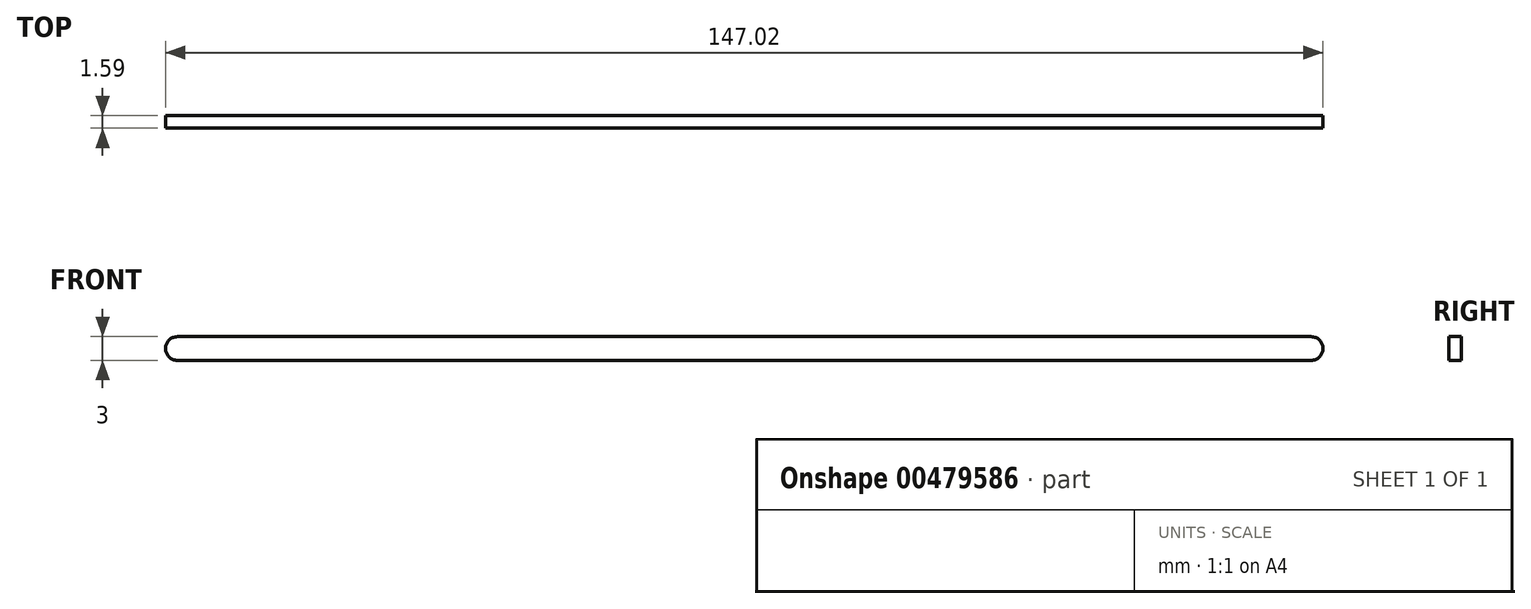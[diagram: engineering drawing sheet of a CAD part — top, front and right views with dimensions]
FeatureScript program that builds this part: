
annotation { "Feature Type Name" : "Feature", "Feature Type Description" : "" }
export const myFeature = defineFeature(function(context is Context, id is Id, definition is map)
    precondition{}
    {
        {
            var Q0;
            Q0=qCreatedBy(makeId("Front.planeOp"),FACE);
            var sketch = newSketch(context, id + "F0", { "sketchPlane" : qUnion([Q0])});
            skLineSegment(sketch, "E0.bottom", {"start": v(72, -1.5) * mm, "end": v(-72, -1.5) * mm});
            skLineSegment(sketch, "E0.top", {"start": v(72, 1.5) * mm, "end": v(-72, 1.5) * mm});
            skPoint(sketch, "E0.middle", {"position": v(0, 0) * mm});
            skArc(sketch, "E1", {"start": v(72, -1.5) * mm, "mid": v(73.5, 0) * mm, "end": v(72, 1.5) * mm});
            skArc(sketch, "E2", {"start": v(-72, 1.5) * mm, "mid": v(-73.5, 0) * mm, "end": v(-72, -1.5) * mm});
            skSolve(sketch);
        }
        {
            var Q0;
            Q0=makeQuery(id+"F0.imprint","IMPRINT",FACE,{"disambiguationData":[TD([[makeQuery(id+"F0.imprint","IMPRINT",EDGE,{"derivedFrom":sQuery(id+"F0.wireOp",EDGE,"E0.bottom")}),-1.0]])]});
            extrude(context, id + "F1", {"entities" : qUnion([Q0]), "depth" : 1.59 * mm});
        }
    });
